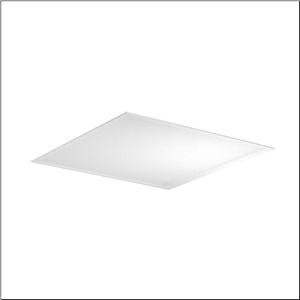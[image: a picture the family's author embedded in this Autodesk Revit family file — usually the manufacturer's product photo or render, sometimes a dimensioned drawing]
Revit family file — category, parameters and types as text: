
# Revit family: apollon_r__31_square_51mp12wd2342_f4b0
name_source: partatom
category: Lighting Fixtures
units: mm (PartAtom-declared; Revit-internal decimal feet)

## family parameters
Cut with Voids When Loaded = No
Host = Face
Light Source = No
Part Type = Normal
Room Calculation Point = No
Round Connector Dimension = Use Diameter
Shared = No

## types (1)
- Apollon® 31 square (1 x LED, 3600 lm, 27.5 W, 3000K)
    Apparent Load = 28 VA
    CIE Flux Codes = 61 87 97 100 100
    Color Rendering = 80
    Color Temperature = 3000K
    Default Elevation = 1800 mm
    Description = Apollon® 31 square, office luminaire, primary optical cover: micro prismatic cover, of PMMA, CAT 2 (L<= 3000cd/m²), light emission: direct distribution, primary light characteristic: symmetric, installation type: lay-in mounting, LED, rated luminous flux: 3.600lm, luminous efficacy: 130lm/W, light colour: 830, colour temperature: 3000K, with terminal, 5-pole, mains connection: 220..240V, AC/DC, 0/50..60Hz, rated input power: 27.5W, housing, of aluminium, traffic white (RAL 9016), module: M600, length: 595mm, width: 595mm, height: 32mm, housing upper side, of sheet steel, galvanised, protection rating (complete): IP20, protection rating (on room side): IP40, insulation class (complete): insulation class II (safety insulation), certification: CE, ENEC, impact resistance: IK03, permissible operating ambient temperature: -20..+40°C, permissible storage temperature: -20..+60°C, packaging unit: 1 piece
    Height = 0 mm  [stored 0 ft]
    Lamp = 1 x LED
    Lamp Light Flux = 3600 lm
    Lamp Power = 27.5 W
    Lamp count = 1
    Length = 595 mm
    Luminous efficacy = 131 lm/W
    Manufacturer = Siteco
    ModVariant = No
    Model = 51MP12WD2342
    Mounting Place = Ceiling
    Mounting Type = Recessed
    Number of Poles = 1
    OnlyDefault = Yes
    Power Factor = 1
    Product Name = Apollon® 31 square
    Product group = office luminaire | ceiling recessed
    ProductGroupID = 401
    Protection Class = Protection class II
    Protection Degree = IP 20
    RLX_Detail_Level = 1
    RLX_Emergency_Light_Flux = 0 lm
    RLX_Emergency_Type = 0
    RLX_Emergency_Type_DB = No
    RlxData = <blob elided: 12493 chars, md5=bbe515af>
    Socket = socket
    Standby Power = 0 W
    System Light Flux = 3600 lm
    System Power = 28 W
    Type Comments = Product without accessories
    Type Image = l_1291035.jpg
    URL = http://relux.com
    VarID = ---
    Voltage = 0 V
    Weight = 0.00 kg
    Width = 595 mm

note: [stored X ft] marks values corroborated as IEEE doubles in the binary element streams (Revit-internal decimal feet)

## geometry (parser evidence)
native form markers: Sweep x11
no freeform markers — native parametric forms only
